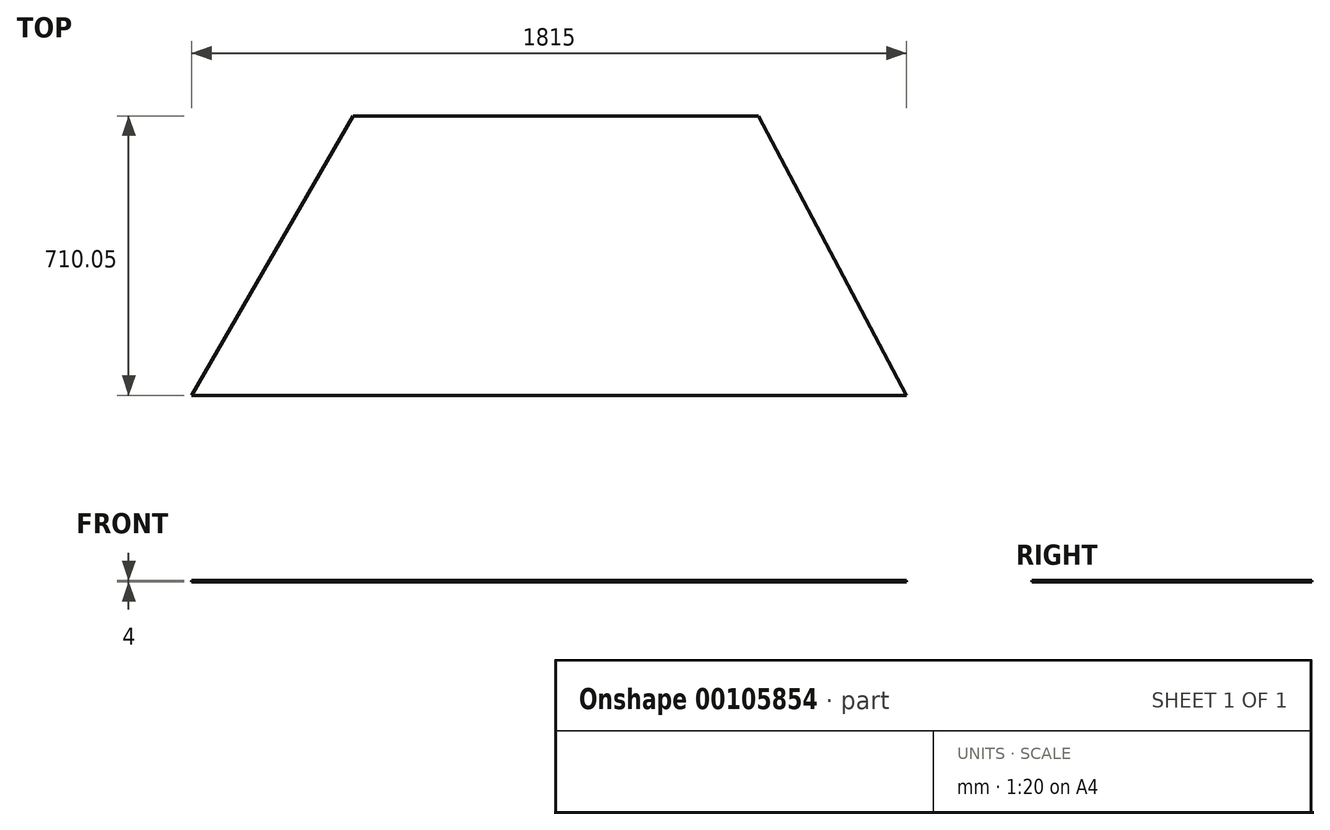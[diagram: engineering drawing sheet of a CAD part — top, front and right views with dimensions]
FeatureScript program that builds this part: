
annotation { "Feature Type Name" : "Feature", "Feature Type Description" : "" }
export const myFeature = defineFeature(function(context is Context, id is Id, definition is map)
    precondition{}
    {
        {
            var Q0;
            Q0=qCreatedBy(makeId("Top.planeOp"),FACE);
            var sketch = newSketch(context, id + "F0", { "sketchPlane" : qUnion([Q0])});
            skLineSegment(sketch, "E0", {"start": v(0, 0) * mm, "end": v(1815, 0) * mm});
            skLineSegment(sketch, "E1", {"start": v(1815, 0) * mm, "end": v(1439.95, 710.05) * mm});
            skLineSegment(sketch, "E2", {"start": v(1439.95, 710.05) * mm, "end": v(409.95, 710.05) * mm});
            skLineSegment(sketch, "E3", {"start": v(0, 0) * mm, "end": v(409.95, 710.05) * mm});
            skSolve(sketch);
        }
        {
            var Q0;
            Q0 = qSketchRegion(id + "F0", true);
            extrude(context, id + "F1", {"entities" : qUnion([Q0]), "depth" : 4 * mm});
        }
    });
